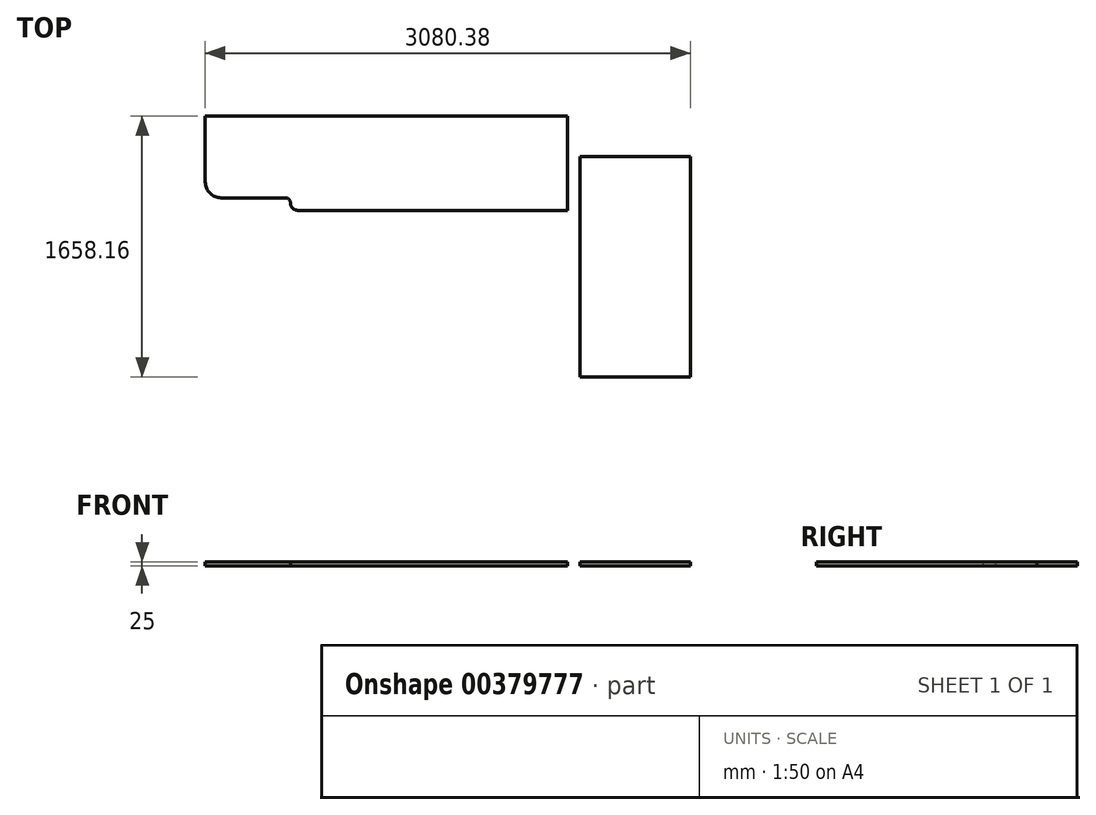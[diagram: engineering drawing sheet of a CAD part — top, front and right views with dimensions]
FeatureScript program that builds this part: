
annotation { "Feature Type Name" : "Feature", "Feature Type Description" : "" }
export const myFeature = defineFeature(function(context is Context, id is Id, definition is map)
    precondition{}
    {
        {
            var Q0;
            Q0=qCreatedBy(makeId("Top.planeOp"),FACE);
            var sketch = newSketch(context, id + "F0", { "sketchPlane" : qUnion([Q0])});
            skLineSegment(sketch, "E0.bottom", {"start": v(-2300, 699.3) * mm, "end": v(0, 699.3) * mm});
            skLineSegment(sketch, "E0.left", {"start": v(-2300, 699.3) * mm, "end": v(-2300, 279.3) * mm});
            skLineSegment(sketch, "E0.right", {"start": v(0, 699.3) * mm, "end": v(0, 99.3) * mm});
            skLineSegment(sketch, "E1", {"start": v(0, 99.3) * mm, "end": v(-1710, 99.3) * mm});
            skLineSegment(sketch, "E2", {"start": v(-2200, 179.3) * mm, "end": v(-1790, 179.3) * mm});
            skLineSegment(sketch, "E3", {"start": v(-1760, 149.3) * mm, "end": v(-1760, 149.3) * mm});
            skPoint(sketch, "E4.visualSharp", {"position": v(-2300, 179.3) * mm});
            skArc(sketch, "E4.filletArc", {"start": v(-2300, 279.3) * mm, "mid": v(-2270.71, 208.59) * mm, "end": v(-2200, 179.3) * mm});
            skPoint(sketch, "E5.visualSharp", {"position": v(-1760, 99.3) * mm});
            skArc(sketch, "E5.filletArc", {"start": v(-1760, 149.3) * mm, "mid": v(-1745.36, 113.94) * mm, "end": v(-1710, 99.3) * mm});
            skPoint(sketch, "E6.visualSharp", {"position": v(-1760, 179.3) * mm});
            skArc(sketch, "E6.filletArc", {"start": v(-1760, 149.3) * mm, "mid": v(-1768.79, 170.51) * mm, "end": v(-1790, 179.3) * mm});
            skSolve(sketch);
        }
        {
            var Q0;
            Q0=qCreatedBy(makeId("Top.planeOp"),FACE);
            var sketch = newSketch(context, id + "F1", { "sketchPlane" : qUnion([Q0])});
            skLineSegment(sketch, "E7.bottom", {"start": v(80.38, 441.14) * mm, "end": v(780.38, 441.14) * mm});
            skLineSegment(sketch, "E7.top", {"start": v(80.38, -958.86) * mm, "end": v(780.38, -958.86) * mm});
            skLineSegment(sketch, "E7.left", {"start": v(80.38, 441.14) * mm, "end": v(80.38, -958.86) * mm});
            skLineSegment(sketch, "E7.right", {"start": v(780.38, 441.14) * mm, "end": v(780.38, -958.86) * mm});
            skSolve(sketch);
        }
        {
            var Q0;
            Q0=makeQuery(id+"F0.imprint","IMPRINT",FACE,{"disambiguationData":[TD([[makeQuery(id+"F0.imprint","IMPRINT",EDGE,{"derivedFrom":sQuery(id+"F0.wireOp",EDGE,"E0.bottom")}),-1.0]])]});
            extrude(context, id + "F2", {"entities" : qUnion([Q0]), "depth" : 25 * mm});
        }
        {
            var Q0;
            Q0=qSketchRegion(id+"F1",true);
            extrude(context, id + "F3", {"entities" : qUnion([Q0]), "depth" : 25 * mm});
        }
    });
